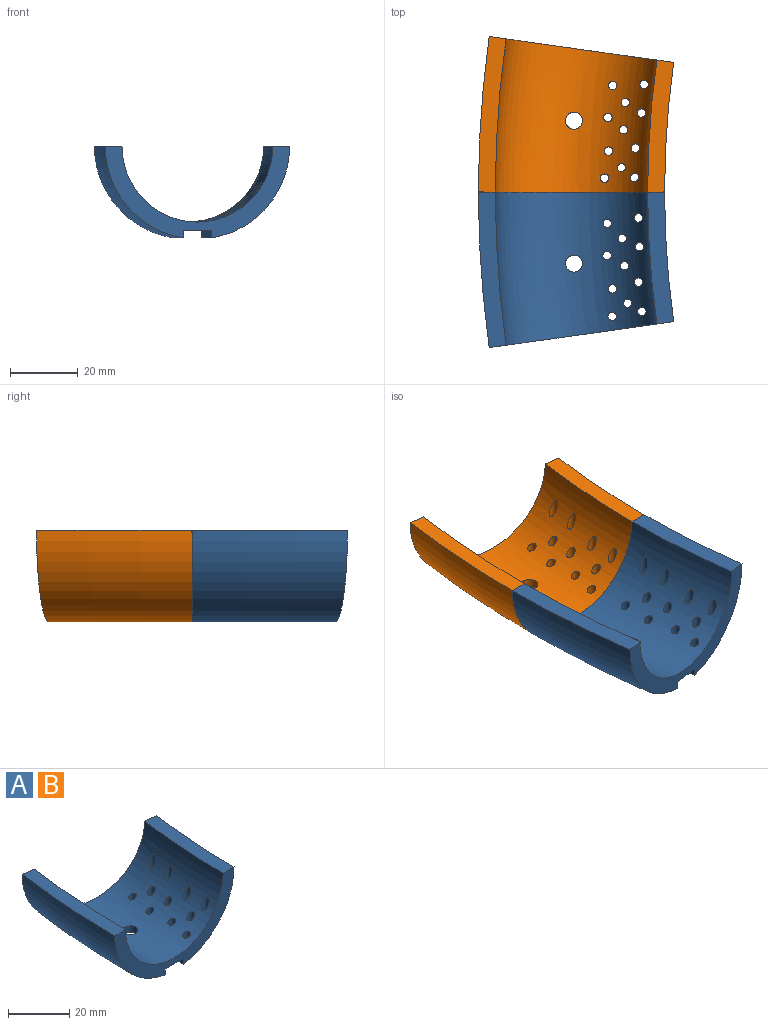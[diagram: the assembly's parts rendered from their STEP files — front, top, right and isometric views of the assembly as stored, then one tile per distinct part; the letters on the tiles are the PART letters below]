
ASSEMBLY  parts=2 mates=1
PART A: 22 faces, bbox 58.5x46x27.5 mm
  f0: torus R=302.53mm, axis (0,0,-1), area 2883.3mm2, adj f2,f3,f4,f9,f10,f11,f12,f13
  f1: torus R=302.53mm, axis (0,0,-1), area 1478mm2, adj f2,f3,f4,f5,f10,f11,f12,f13
  f2: plane 55x27.15mm, normal (0,-1,0), area 372.1mm2, adj f0,f1,f4,f5,f6,f7,f8,f9
  f3: plane 54.46x27.15mm, normal (0.14,0.99,0), area 372.1mm2, adj f0,f1,f4,f5,f6,f7,f8,f9
  f4: plane 38.97x7.68mm, normal (0,0,1), area 193.8mm2, adj f0,f1,f2,f3
  f5: cylinder r=298.4mm len=41.53mm, axis (0,0,-1), area 93.5mm2, adj f1,f2,f3,f6
  f6: plane 42.68x11.15mm, normal (0,0,-1), area 328.7mm2, adj f2,f3,f5,f7,f21
  f7: cylinder r=306.65mm len=42.68mm, axis (0,0,-1), area 96.1mm2, adj f2,f3,f6,f8
  f8: torus R=302.53mm, axis (0,0,-1), area 1752.4mm2, adj f2,f3,f7,f9
  f9: plane 45.93x8.16mm, normal (0,0,1), area 228.7mm2, adj f0,f2,f3,f8
  f10: cylinder r=1.25mm len=6.51mm, axis (0,0,1), area 42.7mm2, adj f0,f1
  f11: cylinder r=1.25mm len=12.14mm, axis (0,0,1), area 66.1mm2, adj f0,f1
  f12: cylinder r=1.25mm len=12.1mm, axis (0,0,1), area 65.9mm2, adj f0,f1
  f13: cylinder r=1.25mm len=8.11mm, axis (0,0,1), area 48.8mm2, adj f0,f1
  f14: cylinder r=1.25mm len=6.69mm, axis (0,0,1), area 43.3mm2, adj f0,f1
  f15: cylinder r=1.25mm len=6.57mm, axis (0,0,1), area 42.9mm2, adj f0,f1
  f16: cylinder r=1.25mm len=8.17mm, axis (0,0,1), area 49.1mm2, adj f0,f1
  f17: cylinder r=1.25mm len=10.68mm, axis (0,0,1), area 59.9mm2, adj f0,f1
  f18: cylinder r=1.25mm len=6.76mm, axis (0,0,1), area 43.6mm2, adj f0,f1
  f19: cylinder r=1.25mm len=10.74mm, axis (0,0,1), area 60.1mm2, adj f0,f1
  f20: cylinder r=1.25mm len=8.11mm, axis (0,0,1), area 48.8mm2, adj f0,f1
  f21: cylinder r=2.5mm len=5mm, axis (0,0,1), area 39.5mm2, adj f0,f6
PART B: same geometry as A
PLACE A rot(axis=(0,0,1),8deg) t=(0,0,0)mm
PLACE B at identity
MATE fastened A.f3 <-> B.f2  axis (0,1,0) through (-302.53,0,0.04)mm
